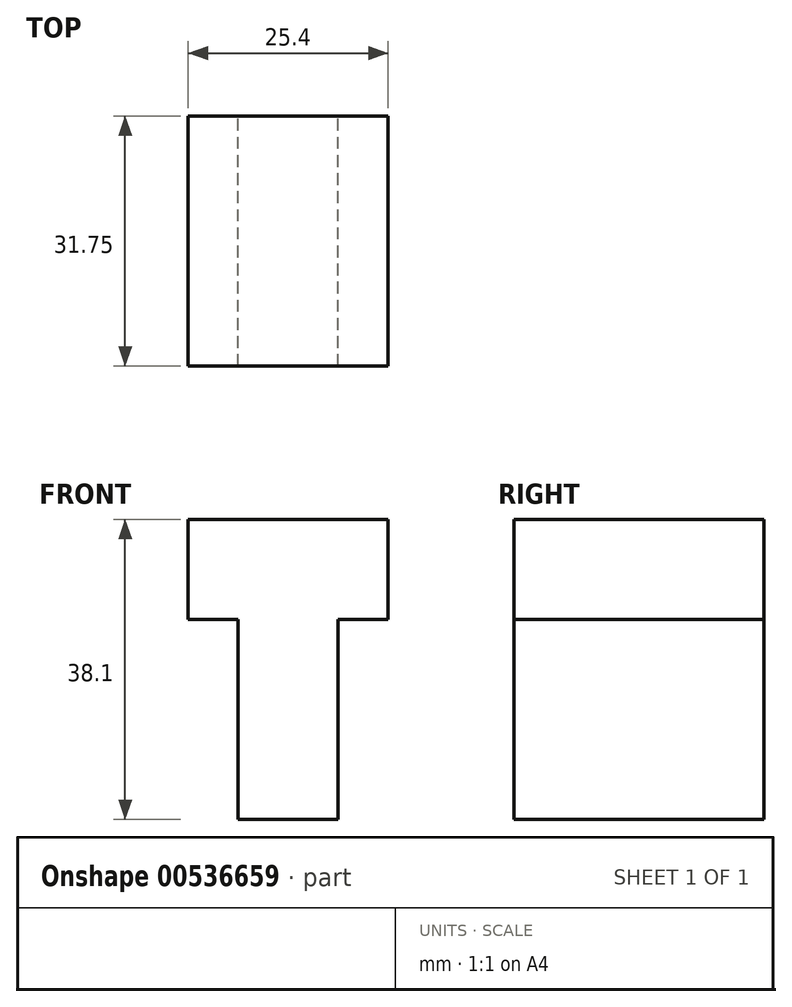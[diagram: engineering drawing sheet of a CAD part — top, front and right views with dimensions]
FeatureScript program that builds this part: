
annotation { "Feature Type Name" : "Feature", "Feature Type Description" : "" }
export const myFeature = defineFeature(function(context is Context, id is Id, definition is map)
    precondition{}
    {
        {
            var Q0;
            Q0=qCreatedBy(makeId("Front.planeOp"),FACE);
            var sketch = newSketch(context, id + "F0", { "sketchPlane" : qUnion([Q0])});
            skLineSegment(sketch, "E0", {"start": v(-61.95, 51.23) * mm, "end": v(-61.95, 38.53) * mm});
            skLineSegment(sketch, "E1", {"start": v(-61.95, 38.53) * mm, "end": v(-55.6, 38.53) * mm});
            skLineSegment(sketch, "E2", {"start": v(-55.6, 38.53) * mm, "end": v(-55.6, 13.13) * mm});
            skLineSegment(sketch, "E3", {"start": v(-55.6, 13.13) * mm, "end": v(-42.9, 13.13) * mm});
            skLineSegment(sketch, "E4", {"start": v(-42.9, 13.13) * mm, "end": v(-42.9, 38.53) * mm});
            skLineSegment(sketch, "E5", {"start": v(-42.9, 38.53) * mm, "end": v(-36.55, 38.53) * mm});
            skLineSegment(sketch, "E6", {"start": v(-36.55, 38.53) * mm, "end": v(-36.55, 51.23) * mm});
            skLineSegment(sketch, "E7", {"start": v(-36.55, 51.23) * mm, "end": v(-61.95, 51.23) * mm});
            skSolve(sketch);
        }
        {
            var Q0;
            Q0=makeQuery(id+"F0.imprint","IMPRINT",FACE,{"disambiguationData":[TD([[makeQuery(id+"F0.imprint","IMPRINT",EDGE,{"derivedFrom":sQuery(id+"F0.wireOp",EDGE,"E0")}),1.0]])]});
            extrude(context, id + "F1", {"entities" : qUnion([Q0]), "depth" : 31.75 * mm, "offsetDistance" : 25.4 * mm});
        }
    });
